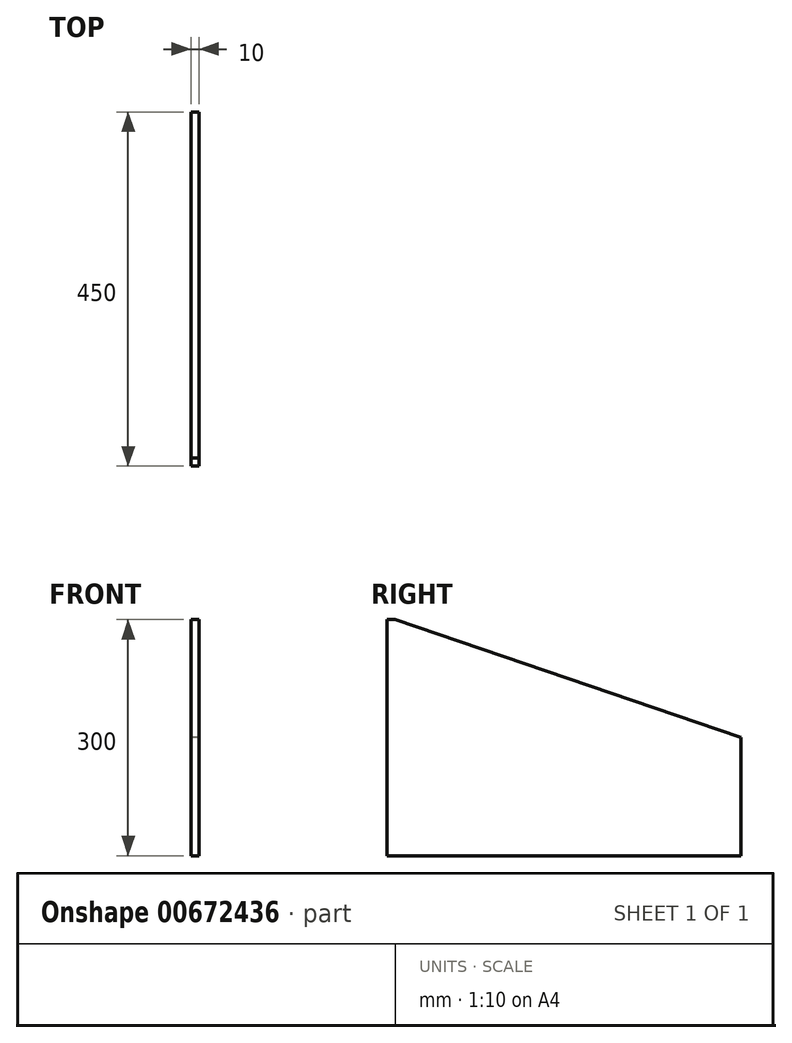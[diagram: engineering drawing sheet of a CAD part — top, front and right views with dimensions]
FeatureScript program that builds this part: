
annotation { "Feature Type Name" : "Feature", "Feature Type Description" : "" }
export const myFeature = defineFeature(function(context is Context, id is Id, definition is map)
    precondition{}
    {
        {
            var Q0;
            Q0=qCreatedBy(makeId("Right.planeOp"),FACE);
            var sketch = newSketch(context, id + "F0", { "sketchPlane" : qUnion([Q0])});
            skLineSegment(sketch, "E0.bottom", {"start": v(-143.9, 0) * mm, "end": v(-133.9, 0) * mm});
            skLineSegment(sketch, "E0.top", {"start": v(-143.9, 300) * mm, "end": v(-133.9, 300) * mm});
            skLineSegment(sketch, "E0.left", {"start": v(-143.9, 0) * mm, "end": v(-143.9, 300) * mm});
            skLineSegment(sketch, "E0.right", {"start": v(-133.9, 0) * mm, "end": v(-133.9, 300) * mm});
            skLineSegment(sketch, "E1.bottom", {"start": v(306.1, 0) * mm, "end": v(117.53, 0) * mm});
            skLineSegment(sketch, "E1.top", {"start": v(306.1, 150) * mm, "end": v(117.53, 150) * mm});
            skLineSegment(sketch, "E1.left", {"start": v(306.1, 0) * mm, "end": v(306.1, 150) * mm});
            skLineSegment(sketch, "E1.right", {"start": v(117.53, 0) * mm, "end": v(117.53, 150) * mm});
            skLineSegment(sketch, "E2", {"start": v(-133.9, 300) * mm, "end": v(306.1, 150) * mm});
            skLineSegment(sketch, "E3", {"start": v(-133.9, 0) * mm, "end": v(117.53, 0) * mm});
            skSolve(sketch);
        }
        {
            var Q0;
            Q0=qSketchRegion(id+"F0",true);
            extrude(context, id + "F1", {"entities" : qUnion([Q0]), "depth" : 10 * mm, "offsetDistance" : 25 * mm});
        }
    });
